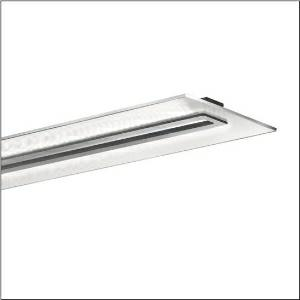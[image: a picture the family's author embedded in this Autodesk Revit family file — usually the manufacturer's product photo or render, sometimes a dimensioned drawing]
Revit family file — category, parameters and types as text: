
# Revit family: vega_r__11_5mn238dle0s3_873d
name_source: partatom
category: Lighting Fixtures
units: mm (PartAtom-declared; Revit-internal decimal feet)

## family parameters
Cut with Voids When Loaded = No
Host = Face
Light Source = No
Part Type = Normal
Room Calculation Point = No
Round Connector Dimension = Use Diameter
Shared = No

## types (1)
- --- (1 x LED 3000K / CRI = 80 (unbekannt), 7300 lm, 3000K)
    Apparent Load = 62 VA
    CIE Flux Codes = 61 86 97 62 100
    Color Rendering = 80
    Color Temperature = 3000K
    Default Elevation = 1800 mm
    Description = Vega® 11, office luminaire, primary light control with prismatic reflector, of PMMA, transparent prismatic structure, CAT 2 (L<= 1500cd/m²), light emission: direct/indirect distribution, primary light characteristic: symmetric, installation type: suspended mounting, surface-mounted, LED, rated luminous flux: 7.300lm, luminous efficacy: 118lm/W, light colour: 830, colour temperature: 3000K, control gear: DALI, with terminal, 3+2-pole, max. 2.5mm², mains connection: 230V, AC, 50Hz, connection cable inclusive, cable length: 1,5m, rated input power: 62W, luminaire housing, rectangular, rounded, of aluminium section, anodised, metallic grey (RAL 9006), length: 1.250mm, width: 350mm, height: 43mm, luminaire housing, lower part, of aluminium section, anodised, metallic grey (RAL 9006), of PC, grey, protection rating (complete): IP20, insulation class (complete): insulation class I (protective earthing), certification: CE, permissible operating ambient temperature: 0..+35°C, standard: EN 50419, packaging unit: 1 piece
    Height = 40 mm  [stored 0.131234 ft]
    Lamp = 1 x LED 3000K / CRI >= 80 (unbekannt)
    Lamp Light Flux = 7300 lm
    Lamp count = 1
    Length = 1250 mm
    Luminous efficacy = 118 lm/W
    Manufacturer = Siteco
    ModVariant = No
    Model = 5MN238DLE0S3
    Mounting Place = Ceiling
    Mounting Type = Pendant
    Number of Poles = 1
    OnlyDefault = Yes
    Power Factor = 1
    Product Name = Vega® 11
    Product group = office luminaire | ceiling pendant
    ProductGroupID = 904
    Protection Class = Protection class I
    Protection Degree = IP 20
    RLX_Detail_Level = 1
    RLX_Emergency_Light_Flux = 0 lm
    RLX_Emergency_Type = 0
    RLX_Emergency_Type_DB = No
    RlxData = <blob elided: 62845 chars, md5=ae8ded5a>
    Socket = socket
    Standby Power = 0 W
    System Light Flux = 7300 lm
    System Power = 62 W
    Type Comments = factory setting: luminous flux: 100 % | dim-lin: 254 | 460 mA
    Type Image = l_1004807.jpg
    URL = http://relux.com
    VarID = @adj_203852
    Voltage = 0 V
    Weight = 0.00 kg
    Width = 350 mm

note: [stored X ft] marks values corroborated as IEEE doubles in the binary element streams (Revit-internal decimal feet)

## geometry (parser evidence)
native form markers: Blend x4, Sweep x11
no freeform markers — native parametric forms only
